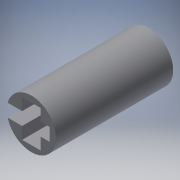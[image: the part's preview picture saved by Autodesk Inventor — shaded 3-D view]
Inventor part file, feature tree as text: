
AUTODESK INVENTOR PART (.ipt)
format: ipt  version: 2016 (Build 200138000, 138)  size: 132,608 bytes
history: native  units: mm
features: other x4, extrude x3, hole x1, sketch x1
ambient origin geometry x8: Origin, YZ Plane, XZ Plane, XY Plane, X Axis, Y Axis, Z Axis, Center Point
bodies: Solid1 (feature_tree)
feature tree (9):
  other  "zero_sketch.ipt"
  extrude  "Extrusion1"  Depth=7.85mm TaperAngle=0.0deg
  extrude  "Extrusion2"  Depth=10.0mm
  extrude  "Extrusion3"  Depth=7.85mm TaperAngle=0.0deg
  hole  "Hole1"  [1 undecoded]
  other  "base+body"
  other  "base+body_1"
  other  "base+body_2"
  sketch  "Sketch5"  dims[d0=10.0mm d1=7.85mm d2=0.0mm d3=10.0mm d4=7.85mm d5=0.0mm d6=10.0mm d7=1.7mm d8=0.0mm d10=0.95mm d11=6.0mm d12=2.5mm d13=1.05mm d14=90.0deg d15=8.0mm d16=20.594885mm]
note: 1 required parameter value undecoded (feature->parameter linkage not recoverable at this tier; creation-order binding heuristic only, values carry confidence <= 0.55)
